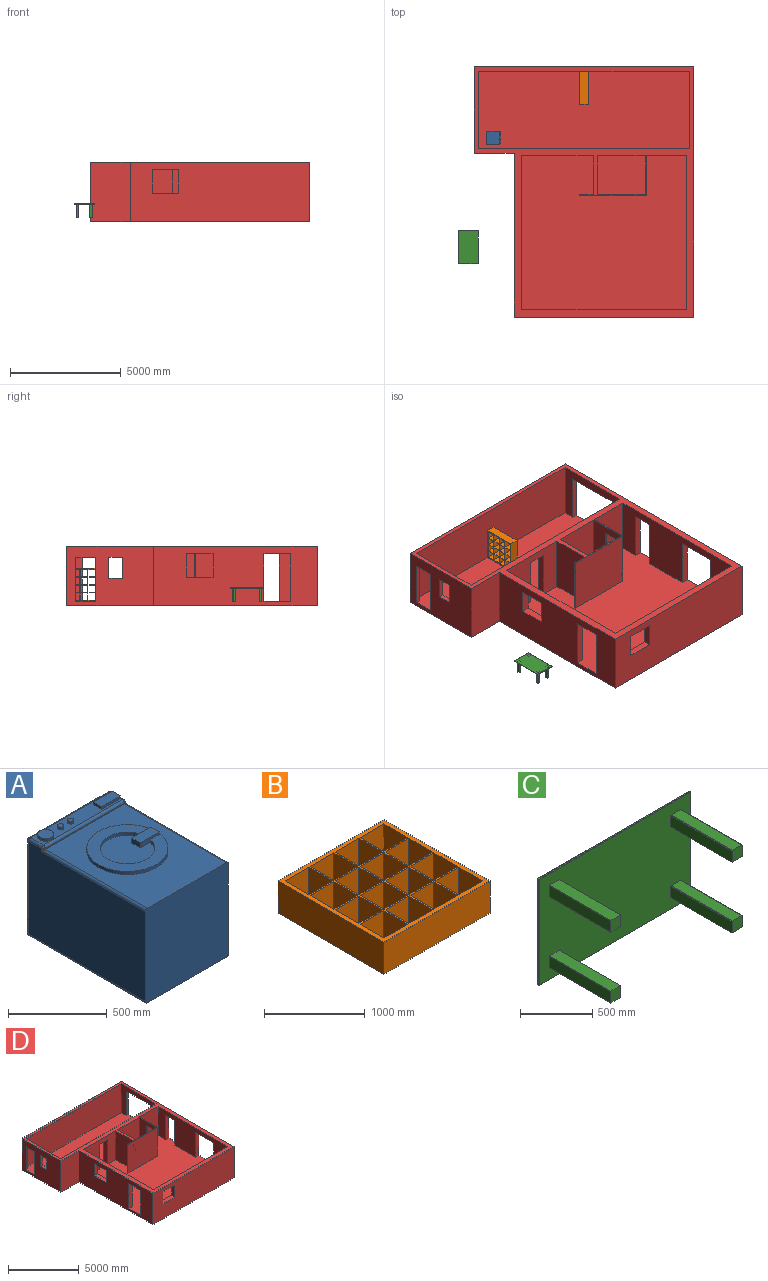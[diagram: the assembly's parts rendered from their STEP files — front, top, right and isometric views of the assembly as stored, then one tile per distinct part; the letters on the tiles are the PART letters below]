
ASSEMBLY  parts=4 mates=6
PART A: 53 faces, bbox 595.1x850x620.8 mm
  f0: plane 277.56x276.88mm, normal (0,0,1), area 60195.2mm2, adj f8,f9
  f1: plane 136.2x60.07mm, normal (0,0,1), area 8181.6mm2, adj f2,f10,f11,f12
  f2: plane 60.07x31.5mm, normal (-1,0,0), area 1892.2mm2, adj f1,f3,f10,f12
  f3: plane 76.52x60.09mm, normal (0,0,-1), area 4529.7mm2, adj f2,f8,f9,f10,f12
  f4: plane 81.27x80.84mm, normal (0,0,1), area 5126.4mm2, adj f13,f14
  f5: plane 30.67x30.56mm, normal (0,0,1), area 730.7mm2, adj f15,f16
  f6: plane 30.67x30.56mm, normal (0,0,1), area 730.7mm2, adj f17,f18
  f7: plane 136.2x60.07mm, normal (0,0,1), area 8181.6mm2, adj f19,f20,f21,f22
  f8: cylinder r=138.42mm len=276.84mm, axis (0,0,1), area 8220.5mm2, adj f0,f3,f9,f12,f24
  f9: cylinder r=138.42mm len=276.84mm, axis (0,0,1), area 8220.5mm2, adj f0,f3,f8,f10,f24
  f10: plane 136.2x31.5mm, normal (0,1,0), area 3298mm2, adj f1,f2,f3,f9,f11,f24
  f11: plane 60.07x15.75mm, normal (1,0,0), area 946.1mm2, adj f1,f10,f12,f24
  f12: plane 136.2x31.5mm, normal (0,-1,0), area 3298mm2, adj f1,f2,f3,f8,f11,f24
  f13: cylinder r=40.4mm len=80.79mm, axis (0,0,1), area 1998.8mm2, adj f4,f14,f29
  f14: cylinder r=40.4mm len=80.79mm, axis (0,0,1), area 1998.8mm2, adj f4,f13,f29
  f15: cylinder r=15.25mm len=30.5mm, axis (0,0,1), area 754.6mm2, adj f5,f16,f29
  f16: cylinder r=15.25mm len=30.5mm, axis (0,0,1), area 754.6mm2, adj f5,f15,f29
  f17: cylinder r=15.25mm len=30.5mm, axis (0,0,1), area 754.6mm2, adj f6,f18,f29
  f18: cylinder r=15.25mm len=30.5mm, axis (0,0,1), area 754.6mm2, adj f6,f17,f29
  f19: plane 60.07x15.75mm, normal (-1,0,0), area 946.1mm2, adj f7,f20,f22,f29
  f20: plane 136.2x15.75mm, normal (0,1,0), area 2145.1mm2, adj f7,f19,f21,f29
  f21: plane 60.07x15.75mm, normal (1,0,0), area 946.1mm2, adj f7,f20,f22,f29
  f22: plane 136.2x15.75mm, normal (0,-1,0), area 2145.1mm2, adj f7,f19,f21,f29
  f23: cylinder r=14.5mm len=566mm, axis (1,0,0), area 12891.5mm2, adj f25,f26,f29,f30
  f24: plane 411.15x410.72mm, normal (0,0,1), area 68613.4mm2, adj f8,f9,f10,f11,f12,f31,f32
  f25: sphere r=14.5mm, area 246.3mm2, adj f23,f33,f34
  f26: sphere r=14.5mm, area 246.3mm2, adj f23,f35,f36
  f27: sphere r=14.5mm, area 246.3mm2, adj f36,f37,f39
  f28: sphere r=14.5mm, area 246.3mm2, adj f34,f38,f39
  f29: plane 566.01x91.01mm, normal (0,0,1), area 36736.7mm2, adj f13,f14,f15,f16,f17,f18,f19,f20
  f30: plane 566x5.5mm, normal (0,-1,0), area 3113mm2, adj f23,f33,f35,f40
  f31: cylinder r=205.34mm len=410.68mm, axis (0,0,1), area 12901.7mm2, adj f24,f32,f40
  f32: cylinder r=205.34mm len=410.68mm, axis (0,0,1), area 12901.7mm2, adj f24,f31,f40
  f33: cylinder r=14.5mm len=20mm, axis (0,0,-1), area 290.4mm2, adj f25,f30,f41,f42
  f34: cylinder r=14.5mm len=91mm, axis (0,-1,0), area 2072.7mm2, adj f25,f28,f29,f42
  f35: cylinder r=14.5mm len=20mm, axis (0,0,-1), area 290.4mm2, adj f26,f30,f43,f44
  f36: cylinder r=14.5mm len=91mm, axis (0,1,0), area 2072.7mm2, adj f26,f27,f29,f44
  f37: cylinder r=14.5mm len=576mm, axis (0,0,1), area 13119.3mm2, adj f27,f44,f45,f47
  f38: cylinder r=14.5mm len=576mm, axis (0,0,-1), area 13119.3mm2, adj f28,f42,f46,f47
  f39: cylinder r=14.5mm len=566mm, axis (-1,0,0), area 12891.5mm2, adj f27,f28,f29,f47
  f40: plane 730x566mm, normal (0,0,1), area 280719.4mm2, adj f30,f31,f32,f41,f43,f49
  f41: cylinder r=14.5mm len=744.5mm, axis (0,-1,0), area 16792mm2, adj f33,f40,f42,f49
  f42: plane 835.5x576mm, normal (-1,0,0), area 466358mm2, adj f33,f34,f38,f41,f48,f49
  f43: cylinder r=14.5mm len=744.5mm, axis (0,1,0), area 16792mm2, adj f35,f40,f44,f49
  f44: plane 835.5x576mm, normal (1,0,0), area 466358mm2, adj f35,f36,f37,f43,f49,f50
  f45: sphere r=14.5mm, area 246.3mm2, adj f37,f50,f51
  f46: sphere r=14.5mm, area 246.3mm2, adj f38,f48,f51
  f47: plane 576x566mm, normal (0,1,0), area 326016mm2, adj f37,f38,f39,f51
  f48: cylinder r=14.5mm len=835.5mm, axis (0,1,0), area 19029.8mm2, adj f42,f46,f49,f52
  f49: plane 595.04x585.04mm, normal (0,-1,0), area 347894.6mm2, adj f40,f41,f42,f43,f44,f48,f50,f52
  f50: cylinder r=14.5mm len=835.5mm, axis (0,-1,0), area 19029.8mm2, adj f44,f45,f49,f52
  f51: cylinder r=14.5mm len=566mm, axis (1,0,0), area 12891.5mm2, adj f45,f46,f47,f52
  f52: plane 835.5x566mm, normal (0,0,-1), area 472893mm2, adj f48,f49,f50,f51
PART B: 70 faces, bbox 1490x1490x390 mm
  f0: plane 1490x1490mm, normal (0,0,1), area 424500mm2, adj f1,f2,f3,f4,f5,f6,f7,f8
  f1: plane 1490x390mm, normal (0,1,0), area 581100mm2, adj f0,f2,f4,f69
  f2: plane 1490x390mm, normal (-1,0,0), area 581100mm2, adj f0,f1,f3,f69
  f3: plane 1490x390mm, normal (0,-1,0), area 581100mm2, adj f0,f2,f4,f69
  f4: plane 1490x390mm, normal (1,0,0), area 581100mm2, adj f0,f1,f3,f69
  f5: plane 390x335mm, normal (0,1,0), area 130650mm2, adj f0,f6,f8,f69
  f6: plane 390x335mm, normal (1,0,0), area 130650mm2, adj f0,f5,f7,f69
  f7: plane 390x335mm, normal (0,-1,0), area 130650mm2, adj f0,f6,f8,f69
  f8: plane 390x335mm, normal (-1,0,0), area 130650mm2, adj f0,f5,f7,f69
  f9: plane 390x335mm, normal (0,1,0), area 130650mm2, adj f0,f10,f12,f69
  f10: plane 390x335mm, normal (1,0,0), area 130650mm2, adj f0,f9,f11,f69
  f11: plane 390x335mm, normal (0,-1,0), area 130650mm2, adj f0,f10,f12,f69
  f12: plane 390x335mm, normal (-1,0,0), area 130650mm2, adj f0,f9,f11,f69
  f13: plane 390x335mm, normal (0,1,0), area 130650mm2, adj f0,f14,f16,f69
  f14: plane 390x335mm, normal (1,0,0), area 130650mm2, adj f0,f13,f15,f69
  f15: plane 390x335mm, normal (0,-1,0), area 130650mm2, adj f0,f14,f16,f69
  f16: plane 390x335mm, normal (-1,0,0), area 130650mm2, adj f0,f13,f15,f69
  f17: plane 390x335mm, normal (0,1,0), area 130650mm2, adj f0,f18,f20,f69
  f18: plane 390x335mm, normal (1,0,0), area 130650mm2, adj f0,f17,f19,f69
  f19: plane 390x335mm, normal (0,-1,0), area 130650mm2, adj f0,f18,f20,f69
  f20: plane 390x335mm, normal (-1,0,0), area 130650mm2, adj f0,f17,f19,f69
  f21: plane 390x335mm, normal (0,1,0), area 130650mm2, adj f0,f22,f24,f69
  f22: plane 390x335mm, normal (1,0,0), area 130650mm2, adj f0,f21,f23,f69
  f23: plane 390x335mm, normal (0,-1,0), area 130650mm2, adj f0,f22,f24,f69
  f24: plane 390x335mm, normal (-1,0,0), area 130650mm2, adj f0,f21,f23,f69
  f25: plane 390x335mm, normal (0,1,0), area 130650mm2, adj f0,f26,f28,f69
  f26: plane 390x335mm, normal (1,0,0), area 130650mm2, adj f0,f25,f27,f69
  f27: plane 390x335mm, normal (0,-1,0), area 130650mm2, adj f0,f26,f28,f69
  f28: plane 390x335mm, normal (-1,0,0), area 130650mm2, adj f0,f25,f27,f69
  f29: plane 390x335mm, normal (0,1,0), area 130650mm2, adj f0,f30,f32,f69
  f30: plane 390x335mm, normal (1,0,0), area 130650mm2, adj f0,f29,f31,f69
  f31: plane 390x335mm, normal (0,-1,0), area 130650mm2, adj f0,f30,f32,f69
  f32: plane 390x335mm, normal (-1,0,0), area 130650mm2, adj f0,f29,f31,f69
  f33: plane 390x335mm, normal (0,1,0), area 130650mm2, adj f0,f34,f36,f69
  f34: plane 390x335mm, normal (1,0,0), area 130650mm2, adj f0,f33,f35,f69
  f35: plane 390x335mm, normal (0,-1,0), area 130650mm2, adj f0,f34,f36,f69
  f36: plane 390x335mm, normal (-1,0,0), area 130650mm2, adj f0,f33,f35,f69
  f37: plane 390x335mm, normal (0,1,0), area 130650mm2, adj f0,f38,f40,f69
  f38: plane 390x335mm, normal (1,0,0), area 130650mm2, adj f0,f37,f39,f69
  f39: plane 390x335mm, normal (0,-1,0), area 130650mm2, adj f0,f38,f40,f69
  f40: plane 390x335mm, normal (-1,0,0), area 130650mm2, adj f0,f37,f39,f69
  f41: plane 390x335mm, normal (0,1,0), area 130650mm2, adj f0,f42,f44,f69
  f42: plane 390x335mm, normal (1,0,0), area 130650mm2, adj f0,f41,f43,f69
  f43: plane 390x335mm, normal (0,-1,0), area 130650mm2, adj f0,f42,f44,f69
  f44: plane 390x335mm, normal (-1,0,0), area 130650mm2, adj f0,f41,f43,f69
  f45: plane 390x335mm, normal (0,1,0), area 130650mm2, adj f0,f46,f48,f69
  f46: plane 390x335mm, normal (1,0,0), area 130650mm2, adj f0,f45,f47,f69
  f47: plane 390x335mm, normal (0,-1,0), area 130650mm2, adj f0,f46,f48,f69
  f48: plane 390x335mm, normal (-1,0,0), area 130650mm2, adj f0,f45,f47,f69
  f49: plane 390x335mm, normal (0,1,0), area 130650mm2, adj f0,f50,f52,f69
  f50: plane 390x335mm, normal (1,0,0), area 130650mm2, adj f0,f49,f51,f69
  f51: plane 390x335mm, normal (0,-1,0), area 130650mm2, adj f0,f50,f52,f69
  f52: plane 390x335mm, normal (-1,0,0), area 130650mm2, adj f0,f49,f51,f69
  f53: plane 390x335mm, normal (0,1,0), area 130650mm2, adj f0,f54,f56,f69
  f54: plane 390x335mm, normal (1,0,0), area 130650mm2, adj f0,f53,f55,f69
  f55: plane 390x335mm, normal (0,-1,0), area 130650mm2, adj f0,f54,f56,f69
  f56: plane 390x335mm, normal (-1,0,0), area 130650mm2, adj f0,f53,f55,f69
  f57: plane 390x335mm, normal (0,1,0), area 130650mm2, adj f0,f58,f60,f69
  f58: plane 390x335mm, normal (1,0,0), area 130650mm2, adj f0,f57,f59,f69
  f59: plane 390x335mm, normal (0,-1,0), area 130650mm2, adj f0,f58,f60,f69
  f60: plane 390x335mm, normal (-1,0,0), area 130650mm2, adj f0,f57,f59,f69
  f61: plane 390x335mm, normal (0,1,0), area 130650mm2, adj f0,f62,f64,f69
  f62: plane 390x335mm, normal (1,0,0), area 130650mm2, adj f0,f61,f63,f69
  f63: plane 390x335mm, normal (0,-1,0), area 130650mm2, adj f0,f62,f64,f69
  f64: plane 390x335mm, normal (-1,0,0), area 130650mm2, adj f0,f61,f63,f69
  f65: plane 390x335mm, normal (0,1,0), area 130650mm2, adj f0,f66,f68,f69
  f66: plane 390x335mm, normal (1,0,0), area 130650mm2, adj f0,f65,f67,f69
  f67: plane 390x335mm, normal (0,-1,0), area 130650mm2, adj f0,f66,f68,f69
  f68: plane 390x335mm, normal (-1,0,0), area 130650mm2, adj f0,f65,f67,f69
  f69: plane 1490x1490mm, normal (0,0,-1), area 424500mm2, adj f1,f2,f3,f4,f5,f6,f7,f8
PART C: 53 faces, bbox 1490x615x900 mm
  f0: plane 1486x896mm, normal (0,1,0), area 1331456mm2, adj f1,f2,f3,f4
  f1: plane 1488x2mm, normal (0,0.71,0.71), area 4205.9mm2, adj f0,f2,f3,f6,f7,f8
  f2: plane 899x2mm, normal (0.71,0.71,0), area 2538.5mm2, adj f0,f1,f4,f8,f9
  f3: plane 898x2mm, normal (-0.71,0.71,0), area 2537.1mm2, adj f0,f1,f4,f5,f6,f10
  f4: plane 1489x2mm, normal (0,0.71,-0.71), area 4207.3mm2, adj f0,f2,f3,f10,f11
  f5: plane 896x11mm, normal (-1,0,0), area 9856mm2, adj f3,f6,f10,f16
  f6: plane 13x2mm, normal (-0.71,0,0.71), area 33.9mm2, adj f1,f3,f5,f7,f16,f17
  f7: plane 1486x11mm, normal (0,0,1), area 16346mm2, adj f1,f6,f8,f17
  f8: plane 13x2mm, normal (0.71,0,0.71), area 33.9mm2, adj f1,f2,f7,f9,f17,f18
  f9: plane 898x11mm, normal (1,0,0), area 9878mm2, adj f2,f8,f11,f18
  f10: plane 13x2mm, normal (-0.71,0,-0.71), area 33.9mm2, adj f3,f4,f5,f11,f16,f19
  f11: plane 1488x11mm, normal (0,0,-1), area 16368mm2, adj f4,f9,f10,f19
  f12: plane 100x100mm, normal (0,-1,0), area 9982mm2, adj f20,f21,f22,f23,f24,f25,f26,f27
  f13: plane 100x100mm, normal (0,-1,0), area 9982mm2, adj f28,f29,f30,f31,f32,f33,f34,f35
  f14: plane 100x100mm, normal (0,-1,0), area 9982mm2, adj f36,f37,f38,f39,f40,f41,f42,f43
  f15: plane 100x100mm, normal (0,-1,0), area 9982mm2, adj f44,f45,f46,f47,f48,f49,f50,f51
  f16: plane 898x2mm, normal (-0.71,-0.71,0), area 2537.1mm2, adj f5,f6,f10,f17,f19,f52
  f17: plane 1488x2mm, normal (0,-0.71,0.71), area 4205.9mm2, adj f6,f7,f8,f16,f18,f52
  f18: plane 899x2mm, normal (0.71,-0.71,0), area 2538.5mm2, adj f8,f9,f17,f19,f52
  f19: plane 1489x2mm, normal (0,-0.71,-0.71), area 4207.3mm2, adj f10,f11,f16,f18,f52
  f20: plane 600x94mm, normal (0,0,1), area 56400mm2, adj f12,f21,f27,f52
  f21: plane 600x3mm, normal (-0.71,0,0.71), area 2545.6mm2, adj f12,f20,f22,f52
  f22: plane 600x94mm, normal (-1,0,0), area 56400mm2, adj f12,f21,f23,f52
  f23: plane 600x3mm, normal (-0.71,0,-0.71), area 2545.6mm2, adj f12,f22,f24,f52
  f24: plane 600x94mm, normal (0,0,-1), area 56400mm2, adj f12,f23,f25,f52
  f25: plane 600x3mm, normal (0.71,0,-0.71), area 2545.6mm2, adj f12,f24,f26,f52
  f26: plane 600x94mm, normal (1,0,0), area 56400mm2, adj f12,f25,f27,f52
  f27: plane 600x3mm, normal (0.71,0,0.71), area 2545.6mm2, adj f12,f20,f26,f52
  f28: plane 600x94mm, normal (0,0,1), area 56400mm2, adj f13,f29,f35,f52
  f29: plane 600x3mm, normal (-0.71,0,0.71), area 2545.6mm2, adj f13,f28,f30,f52
  f30: plane 600x94mm, normal (-1,0,0), area 56400mm2, adj f13,f29,f31,f52
  f31: plane 600x3mm, normal (-0.71,0,-0.71), area 2545.6mm2, adj f13,f30,f32,f52
  f32: plane 600x94mm, normal (0,0,-1), area 56400mm2, adj f13,f31,f33,f52
  f33: plane 600x3mm, normal (0.71,0,-0.71), area 2545.6mm2, adj f13,f32,f34,f52
  f34: plane 600x94mm, normal (1,0,0), area 56400mm2, adj f13,f33,f35,f52
  f35: plane 600x3mm, normal (0.71,0,0.71), area 2545.6mm2, adj f13,f28,f34,f52
  f36: plane 600x94mm, normal (0,0,1), area 56400mm2, adj f14,f37,f43,f52
  f37: plane 600x3mm, normal (-0.71,0,0.71), area 2545.6mm2, adj f14,f36,f38,f52
  f38: plane 600x94mm, normal (-1,0,0), area 56400mm2, adj f14,f37,f39,f52
  f39: plane 600x3mm, normal (-0.71,0,-0.71), area 2545.6mm2, adj f14,f38,f40,f52
  f40: plane 600x94mm, normal (0,0,-1), area 56400mm2, adj f14,f39,f41,f52
  f41: plane 600x3mm, normal (0.71,0,-0.71), area 2545.6mm2, adj f14,f40,f42,f52
  f42: plane 600x94mm, normal (1,0,0), area 56400mm2, adj f14,f41,f43,f52
  f43: plane 600x3mm, normal (0.71,0,0.71), area 2545.6mm2, adj f14,f36,f42,f52
  f44: plane 600x94mm, normal (0,0,1), area 56400mm2, adj f15,f45,f51,f52
  f45: plane 600x3mm, normal (-0.71,0,0.71), area 2545.6mm2, adj f15,f44,f46,f52
  f46: plane 600x94mm, normal (-1,0,0), area 56400mm2, adj f15,f45,f47,f52
  f47: plane 600x3mm, normal (-0.71,0,-0.71), area 2545.6mm2, adj f15,f46,f48,f52
  f48: plane 600x94mm, normal (0,0,-1), area 56400mm2, adj f15,f47,f49,f52
  f49: plane 600x3mm, normal (0.71,0,-0.71), area 2545.6mm2, adj f15,f48,f50,f52
  f50: plane 600x94mm, normal (1,0,0), area 56400mm2, adj f15,f49,f51,f52
  f51: plane 600x3mm, normal (0.71,0,0.71), area 2545.6mm2, adj f15,f44,f50,f52
  f52: plane 1486x896mm, normal (0,-1,0), area 1291528mm2, adj f16,f17,f18,f19,f20,f21,f22,f23
PART D: 60 faces, bbox 9900x11300x2700 mm
  f0: plane 11300x9900mm, normal (0,0,-1), area 98550000mm2, adj f35,f36,f37,f38,f39,f40
  f1: plane 2120x200mm, normal (0,-1,0), area 424000mm2, adj f2,f34,f38,f41
  f2: plane 2500x200mm, normal (0,0,-1), area 500000mm2, adj f1,f3,f38,f41
  f3: plane 2120x200mm, normal (0,1,0), area 424000mm2, adj f2,f34,f38,f41
  f4: plane 2000x200mm, normal (0,1,0), area 400000mm2, adj f5,f34,f40,f43
  f5: plane 900x200mm, normal (0,0,-1), area 180000mm2, adj f4,f6,f40,f43
  f6: plane 2000x200mm, normal (0,-1,0), area 400000mm2, adj f5,f34,f40,f43
  f7: plane 600x200mm, normal (0,0,-1), area 120000mm2, adj f8,f10,f40,f43
  f8: plane 950x200mm, normal (0,-1,0), area 190000mm2, adj f7,f9,f40,f43
  f9: plane 600x200mm, normal (0,0,1), area 120000mm2, adj f8,f10,f40,f43
  f10: plane 950x200mm, normal (0,1,0), area 190000mm2, adj f7,f9,f40,f43
  f11: plane 1050x320mm, normal (-1,0,0), area 336000mm2, adj f12,f14,f37,f45
  f12: plane 1200x320mm, normal (0,0,-1), area 384000mm2, adj f11,f13,f37,f45
  f13: plane 1050x320mm, normal (1,0,0), area 336000mm2, adj f12,f14,f37,f45
  f14: plane 1200x320mm, normal (0,0,1), area 384000mm2, adj f11,f13,f37,f45
  f15: plane 2150x342.18mm, normal (0,1,0), area 735684.8mm2, adj f16,f34,f36,f46
  f16: plane 1200x342.18mm, normal (0,0,-1), area 410614.8mm2, adj f15,f17,f36,f46
  f17: plane 2150x342.18mm, normal (0,-1,0), area 735684.8mm2, adj f16,f34,f36,f46
  f18: plane 1050x342.18mm, normal (0,1,0), area 359287.9mm2, adj f19,f21,f36,f46
  f19: plane 1200x342.18mm, normal (0,0,-1), area 410614.8mm2, adj f18,f20,f36,f46
  f20: plane 1050x342.18mm, normal (0,-1,0), area 359287.9mm2, adj f19,f21,f36,f46
  f21: plane 1200x342.18mm, normal (0,0,1), area 410614.8mm2, adj f18,f20,f36,f46
  f22: plane 2150x320mm, normal (1,0,0), area 688000mm2, adj f23,f34,f42,f47
  f23: plane 800x320mm, normal (0,0,-1), area 256000mm2, adj f22,f24,f42,f47
  f24: plane 2150x320mm, normal (-1,0,0), area 688000mm2, adj f23,f34,f42,f47
  f25: plane 2150x320mm, normal (0,-1,0), area 688000mm2, adj f26,f34,f38,f54
  f26: plane 900x320mm, normal (0,0,-1), area 288000mm2, adj f25,f27,f38,f54
  f27: plane 2150x320mm, normal (0,1,0), area 688000mm2, adj f26,f34,f38,f54
  f28: plane 2150x320mm, normal (0,-1,0), area 688000mm2, adj f29,f34,f38,f54
  f29: plane 1800x320mm, normal (0,0,-1), area 576000mm2, adj f28,f30,f38,f54
  f30: plane 2150x320mm, normal (0,1,0), area 688000mm2, adj f29,f34,f38,f54
  f31: plane 2150x50mm, normal (0,-1,0), area 107500mm2, adj f32,f34,f52,f55
  f32: plane 800x50mm, normal (0,0,-1), area 40000mm2, adj f31,f33,f52,f55
  f33: plane 2150x50mm, normal (0,1,0), area 107500mm2, adj f32,f34,f52,f55
  f34: plane 10780x9900mm, normal (0,0,1), area 86680349mm2, adj f1,f3,f4,f6,f15,f17,f22,f24
  f35: plane 2700x1800mm, normal (0,-1,0), area 4860000mm2, adj f0,f36,f40,f59
  f36: plane 7400x2700mm, normal (-1,0,0), area 16140000mm2, adj f0,f15,f16,f17,f18,f19,f20,f21
  f37: plane 8100x2700mm, normal (0,-1,0), area 20610000mm2, adj f0,f11,f12,f13,f14,f36,f38,f59
  f38: plane 11300x2700mm, normal (1,0,0), area 19405000mm2, adj f0,f1,f2,f3,f25,f26,f27,f28
  f39: plane 9900x2700mm, normal (0,1,0), area 26730000mm2, adj f0,f38,f40,f59
  f40: plane 3900x2700mm, normal (-1,0,0), area 8160000mm2, adj f0,f4,f5,f6,f7,f8,f9,f10
  f41: plane 3500x2500mm, normal (-1,0,0), area 3450000mm2, adj f1,f2,f3,f34,f42,f44,f59
  f42: plane 9500x2500mm, normal (0,1,0), area 22030000mm2, adj f22,f23,f24,f34,f41,f43,f59
  f43: plane 3500x2500mm, normal (1,0,0), area 6380000mm2, adj f4,f5,f6,f7,f8,f9,f10,f34
  f44: plane 9500x2500mm, normal (0,-1,0), area 23750000mm2, adj f34,f41,f43,f59
  f45: plane 7437.82x2500mm, normal (0,1,0), area 17334552.5mm2, adj f11,f12,f13,f14,f34,f46,f54,f59
  f46: plane 6960x2500mm, normal (1,0,0), area 13560000mm2, adj f15,f16,f17,f18,f19,f20,f21,f34
  f47: plane 3220x2500mm, normal (0,-1,0), area 6330000mm2, adj f22,f23,f24,f34,f46,f48,f59
  f48: plane 2500x1750mm, normal (-1,0,0), area 4375000mm2, adj f34,f47,f49,f59
  f49: plane 2500x600mm, normal (0,1,0), area 1500000mm2, adj f34,f48,f50,f59
  f50: plane 2500x50mm, normal (-1,0,0), area 125000mm2, adj f34,f49,f51,f59
  f51: plane 3000x2500mm, normal (0,-1,0), area 7500000mm2, adj f34,f50,f52,f59
  f52: plane 2500x1800mm, normal (1,0,0), area 2780000mm2, adj f31,f32,f33,f34,f51,f53,f59
  f53: plane 2500x1817.82mm, normal (0,-1,0), area 4544552.5mm2, adj f34,f52,f54,f59
  f54: plane 6960x2500mm, normal (-1,0,0), area 11595000mm2, adj f25,f26,f27,f28,f29,f30,f34,f45
  f55: plane 2500x1750mm, normal (-1,0,0), area 2655000mm2, adj f31,f32,f33,f34,f56,f58,f59
  f56: plane 2500x2150mm, normal (0,1,0), area 5375000mm2, adj f34,f55,f57,f59
  f57: plane 2500x1750mm, normal (1,0,0), area 4375000mm2, adj f34,f56,f58,f59
  f58: plane 2500x2150mm, normal (0,-1,0), area 5375000mm2, adj f34,f55,f57,f59
  f59: plane 11300x9900mm, normal (0,0,1), area 14120265.8mm2, adj f35,f36,f37,f38,f39,f40,f41,f42
PLACE A rot(axis=(0.58,0.58,0.58),120deg) t=(-8970.95,103.19,1805.37)mm
PLACE B rot(axis=(0.58,0.58,0.58),120deg) t=(-5054.26,2372.13,2125.37)mm
PLACE C rot(axis=(0.58,0.58,0.58),120deg) t=(-10076.82,-4827.15,1980.37)mm
PLACE D t=(-4804.07,-2657.08,1380.37)mm fixed
MATE planar B.f4 <-> D.f44  axis (0,1,0) through (-4859.26,3117.13,2125.37)mm
MATE planar A.f49 <-> D.f34  axis (0,0,-1) through (-8970.95,103.19,1380.37)mm
MATE planar C.f14 <-> D.f34  axis (0,0,-1) through (-9776.82,-4232.15,1380.37)mm
MATE planar B.f3 <-> D.f34  axis (0,0,-1) through (-4859.26,2372.13,1380.37)mm
MATE parallel C.f11 <-> D.f43  axis (-1,0,0) through (-10526.82,-4826.15,1987.87)mm
MATE parallel A.f44 <-> D.f42  axis (0,1,0) through (-8969.82,400.69,1799.57)mm
